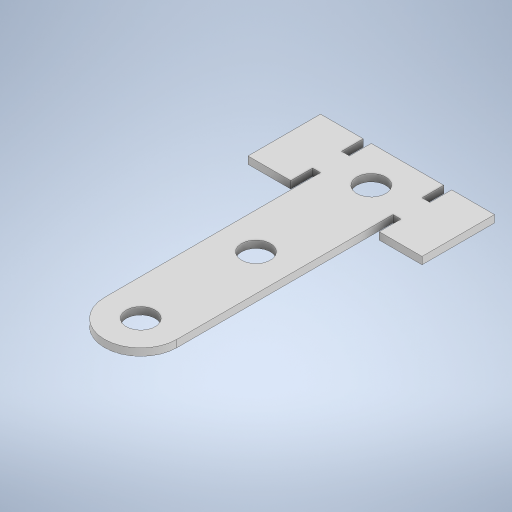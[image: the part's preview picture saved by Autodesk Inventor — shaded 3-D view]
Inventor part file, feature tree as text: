
AUTODESK INVENTOR PART (.ipt)
format: ipt  version: 2024.1 (Build 281209000, 209)  size: 290,304 bytes
history: native  units: mm
features: extrude x3, sketch x3, other x1, projected_geometry x1
ambient origin geometry x8: Origin, YZ Plane, XZ Plane, XY Plane, X Axis, Y Axis, Z Axis, Center Point
bodies: Body1 (feature_tree)
feature tree (8):
  other  "ソリッド1"
  extrude  "押し出し1"  Depth=114.0mm
  extrude  "押し出し2"  Depth=45.0mm
  extrude  "押し出し3"  Depth=150.0mm
  sketch  "スケッチ1"
  sketch  "スケッチ2"
  projected_geometry  "投影ループ1"
  sketch  "スケッチ3"
